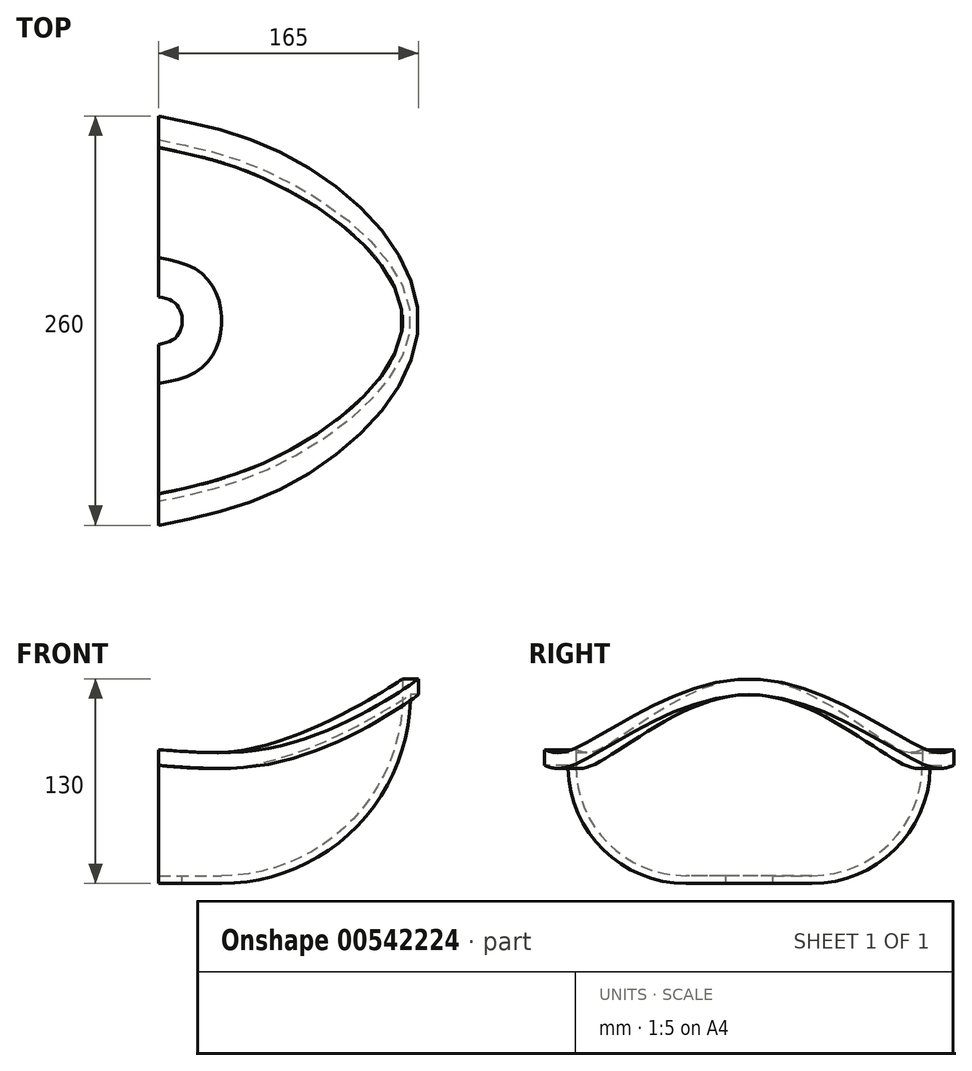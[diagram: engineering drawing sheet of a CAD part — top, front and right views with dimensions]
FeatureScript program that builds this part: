
annotation { "Feature Type Name" : "Feature", "Feature Type Description" : "" }
export const myFeature = defineFeature(function(context is Context, id is Id, definition is map)
    precondition{}
    {
        {
            var Q0;
            Q0=qCreatedBy(makeId("Front.planeOp"),FACE);
            var sketch = newSketch(context, id + "F0", { "sketchPlane" : qUnion([Q0])});
            skLineSegment(sketch, "E0.bottom", {"start": v(15, 5) * mm, "end": v(40, 5) * mm});
            skLineSegment(sketch, "E0.top", {"start": v(15, 0) * mm, "end": v(40, 0) * mm});
            skLineSegment(sketch, "E0.left", {"start": v(15, 5) * mm, "end": v(15, 0) * mm});
            skLineSegment(sketch, "E0.right", {"start": v(40, 5) * mm, "end": v(40, 0) * mm, "construction": true});
            skLineSegment(sketch, "E1.bottom", {"start": v(155, 130) * mm, "end": v(165, 130) * mm});
            skLineSegment(sketch, "E1.top", {"start": v(160, 120) * mm, "end": v(165, 120) * mm});
            skLineSegment(sketch, "E1.left", {"start": v(155, 130) * mm, "end": v(155, 120) * mm});
            skLineSegment(sketch, "E1.right", {"start": v(165, 130) * mm, "end": v(165, 120) * mm});
            skArc(sketch, "E2", {"start": v(40, 0) * mm, "mid": v(124.85, 35.15) * mm, "end": v(160, 120) * mm});
            skArc(sketch, "E3", {"start": v(40, 5) * mm, "mid": v(121.32, 38.68) * mm, "end": v(155, 120) * mm});
            skLineSegment(sketch, "E4", {"start": v(0, 0) * mm, "end": v(0, 50) * mm, "construction": true});
            skSolve(sketch);
        }
        {
            var Q0;
            Q0=sQuery(id+"F0.wireOp",EDGE,"E4");
            cPlane(context, id + "F1", {"entities" : qUnion([Q0]), "cplaneType" : CPlaneType.LINE_ANGLE, "offset" : 25 * mm, "angle" : 330 * degree, "width" : 150 * mm, "height" : 150 * mm});
        }
        {
            var Q0;
            Q0=qCreatedBy(id+"F1.planeOp",FACE);
            var sketch = newSketch(context, id + "F2", { "sketchPlane" : qUnion([Q0])});
            skLineSegment(sketch, "E5.bottom", {"start": v(15, 5) * mm, "end": v(40, 5) * mm});
            skLineSegment(sketch, "E5.top", {"start": v(15, 0) * mm, "end": v(40, 0) * mm});
            skLineSegment(sketch, "E5.left", {"start": v(15, 5) * mm, "end": v(15, 0) * mm});
            skLineSegment(sketch, "E5.right", {"start": v(40, 5) * mm, "end": v(40, 0) * mm, "construction": true});
            skLineSegment(sketch, "E6.bottom", {"start": v(110, 85) * mm, "end": v(130, 85) * mm});
            skLineSegment(sketch, "E6.top", {"start": v(115, 75) * mm, "end": v(130, 75) * mm});
            skLineSegment(sketch, "E6.left", {"start": v(110, 85) * mm, "end": v(110, 75) * mm});
            skLineSegment(sketch, "E6.right", {"start": v(130, 85) * mm, "end": v(130, 75) * mm});
            skArc(sketch, "E7", {"start": v(40, 0) * mm, "mid": v(93.03, 21.97) * mm, "end": v(115, 75) * mm});
            skArc(sketch, "E8", {"start": v(40, 5) * mm, "mid": v(89.5, 25.5) * mm, "end": v(110, 75) * mm});
            skLineSegment(sketch, "E9", {"start": v(0, 0) * mm, "end": v(0, 50) * mm, "construction": true});
            skSolve(sketch);
        }
        {
            var Q0;
            Q0=sQuery(id+"F2.wireOp",EDGE,"E9");
            cPlane(context, id + "F3", {"entities" : qUnion([Q0]), "cplaneType" : CPlaneType.LINE_ANGLE, "offset" : 25 * mm, "angle" : 150 * degree, "oppositeDirection" : true, "width" : 150 * mm, "height" : 150 * mm});
        }
        {
            var Q0;
            Q0=qCreatedBy(id+"F3.planeOp",FACE);
            var sketch = newSketch(context, id + "F4", { "sketchPlane" : qUnion([Q0])});
            skLineSegment(sketch, "E10.bottom", {"start": v(15, 5) * mm, "end": v(40, 5) * mm});
            skLineSegment(sketch, "E10.top", {"start": v(15, 0) * mm, "end": v(40, 0) * mm});
            skLineSegment(sketch, "E10.left", {"start": v(15, 5) * mm, "end": v(15, 0) * mm});
            skLineSegment(sketch, "E10.right", {"start": v(40, 5) * mm, "end": v(40, 0) * mm, "construction": true});
            skLineSegment(sketch, "E11.bottom", {"start": v(110, 85) * mm, "end": v(130, 85) * mm});
            skLineSegment(sketch, "E11.top", {"start": v(115, 75) * mm, "end": v(130, 75) * mm});
            skLineSegment(sketch, "E11.left", {"start": v(110, 85) * mm, "end": v(110, 75) * mm});
            skLineSegment(sketch, "E11.right", {"start": v(130, 85) * mm, "end": v(130, 75) * mm});
            skArc(sketch, "E12", {"start": v(40, 0) * mm, "mid": v(93.03, 21.97) * mm, "end": v(115, 75) * mm});
            skArc(sketch, "E13", {"start": v(40, 5) * mm, "mid": v(89.5, 25.5) * mm, "end": v(110, 75) * mm});
            skLineSegment(sketch, "E14", {"start": v(0, 0) * mm, "end": v(0, 50) * mm, "construction": true});
            skSolve(sketch);
        }
        {
            var Q0;
            Q0=qCreatedBy(makeId("Right.planeOp"),FACE);
            var sketch = newSketch(context, id + "F5", { "sketchPlane" : qUnion([Q0])});
            skLineSegment(sketch, "E15.bottom", {"start": v(15, 5) * mm, "end": v(40, 5) * mm});
            skLineSegment(sketch, "E15.top", {"start": v(15, 0) * mm, "end": v(40, 0) * mm});
            skLineSegment(sketch, "E15.left", {"start": v(15, 5) * mm, "end": v(15, 0) * mm});
            skLineSegment(sketch, "E15.right", {"start": v(40, 5) * mm, "end": v(40, 0) * mm, "construction": true});
            skLineSegment(sketch, "E16.bottom", {"start": v(110, 85) * mm, "end": v(130, 85) * mm});
            skLineSegment(sketch, "E16.top", {"start": v(115, 75) * mm, "end": v(130, 75) * mm});
            skLineSegment(sketch, "E16.left", {"start": v(110, 85) * mm, "end": v(110, 75) * mm});
            skLineSegment(sketch, "E16.right", {"start": v(130, 85) * mm, "end": v(130, 75) * mm});
            skArc(sketch, "E17", {"start": v(40, 0) * mm, "mid": v(93.03, 21.97) * mm, "end": v(115, 75) * mm});
            skArc(sketch, "E18", {"start": v(40, 5) * mm, "mid": v(89.5, 25.5) * mm, "end": v(110, 75) * mm});
            skLineSegment(sketch, "E19", {"start": v(0, 0) * mm, "end": v(0, 50) * mm, "construction": true});
            skSolve(sketch);
        }
        {
            var Q0;
            Q0=sQuery(id+"F5.wireOp",EDGE,"E19");
            cPlane(context, id + "F6", {"entities" : qUnion([Q0]), "cplaneType" : CPlaneType.LINE_ANGLE, "offset" : 25 * mm, "angle" : 180 * degree, "width" : 150 * mm, "height" : 150 * mm});
        }
        {
            var Q0;
            Q0=qCreatedBy(id+"F6.planeOp",FACE);
            var sketch = newSketch(context, id + "F7", { "sketchPlane" : qUnion([Q0])});
            skLineSegment(sketch, "E20.bottom", {"start": v(15, 5) * mm, "end": v(40, 5) * mm});
            skLineSegment(sketch, "E20.top", {"start": v(15, 0) * mm, "end": v(40, 0) * mm});
            skLineSegment(sketch, "E20.left", {"start": v(15, 5) * mm, "end": v(15, 0) * mm});
            skLineSegment(sketch, "E20.right", {"start": v(40, 5) * mm, "end": v(40, 0) * mm, "construction": true});
            skLineSegment(sketch, "E21.bottom", {"start": v(110, 85) * mm, "end": v(130, 85) * mm});
            skLineSegment(sketch, "E21.top", {"start": v(115, 75) * mm, "end": v(130, 75) * mm});
            skLineSegment(sketch, "E21.left", {"start": v(110, 85) * mm, "end": v(110, 75) * mm});
            skLineSegment(sketch, "E21.right", {"start": v(130, 85) * mm, "end": v(130, 75) * mm});
            skArc(sketch, "E22", {"start": v(40, 0) * mm, "mid": v(93.03, 21.97) * mm, "end": v(115, 75) * mm});
            skArc(sketch, "E23", {"start": v(40, 5) * mm, "mid": v(89.5, 25.5) * mm, "end": v(110, 75) * mm});
            skLineSegment(sketch, "E24", {"start": v(0, 0) * mm, "end": v(0, 50) * mm, "construction": true});
            skSolve(sketch);
        }
        {
            var Q0;
            Q0=makeQuery(id+"F5.imprint","IMPRINT",FACE,{"disambiguationData":[TD([[makeQuery(id+"F5.imprint","IMPRINT",EDGE,{"derivedFrom":sQuery(id+"F5.wireOp",EDGE,"E15.bottom")}),-1.0]])]});
            var Q1;
            Q1=makeQuery(id+"F2.imprint","IMPRINT",FACE,{"disambiguationData":[TD([[makeQuery(id+"F2.imprint","IMPRINT",EDGE,{"derivedFrom":sQuery(id+"F2.wireOp",EDGE,"E5.bottom")}),-1.0]])]});
            var Q2;
            Q2=makeQuery(id+"F0.imprint","IMPRINT",FACE,{"disambiguationData":[TD([[makeQuery(id+"F0.imprint","IMPRINT",EDGE,{"derivedFrom":sQuery(id+"F0.wireOp",EDGE,"E0.bottom")}),-1.0]])]});
            var Q3;
            Q3=makeQuery(id+"F4.imprint","IMPRINT",FACE,{"disambiguationData":[TD([[makeQuery(id+"F4.imprint","IMPRINT",EDGE,{"derivedFrom":sQuery(id+"F4.wireOp",EDGE,"E10.bottom")}),-1.0]])]});
            var Q4;
            Q4=makeQuery(id+"F7.imprint","IMPRINT",FACE,{"disambiguationData":[TD([[makeQuery(id+"F7.imprint","IMPRINT",EDGE,{"derivedFrom":sQuery(id+"F7.wireOp",EDGE,"E20.bottom")}),-1.0]])]});
            loft(context, id + "F8", {"sheetProfilesArray" : [{ "sheetProfileEntities" : qUnion([Q0]) }, { "sheetProfileEntities" : qUnion([Q1]) }, { "sheetProfileEntities" : qUnion([Q2]) }, { "sheetProfileEntities" : qUnion([Q3]) }, { "sheetProfileEntities" : qUnion([Q4]) }]});
        }
    });
